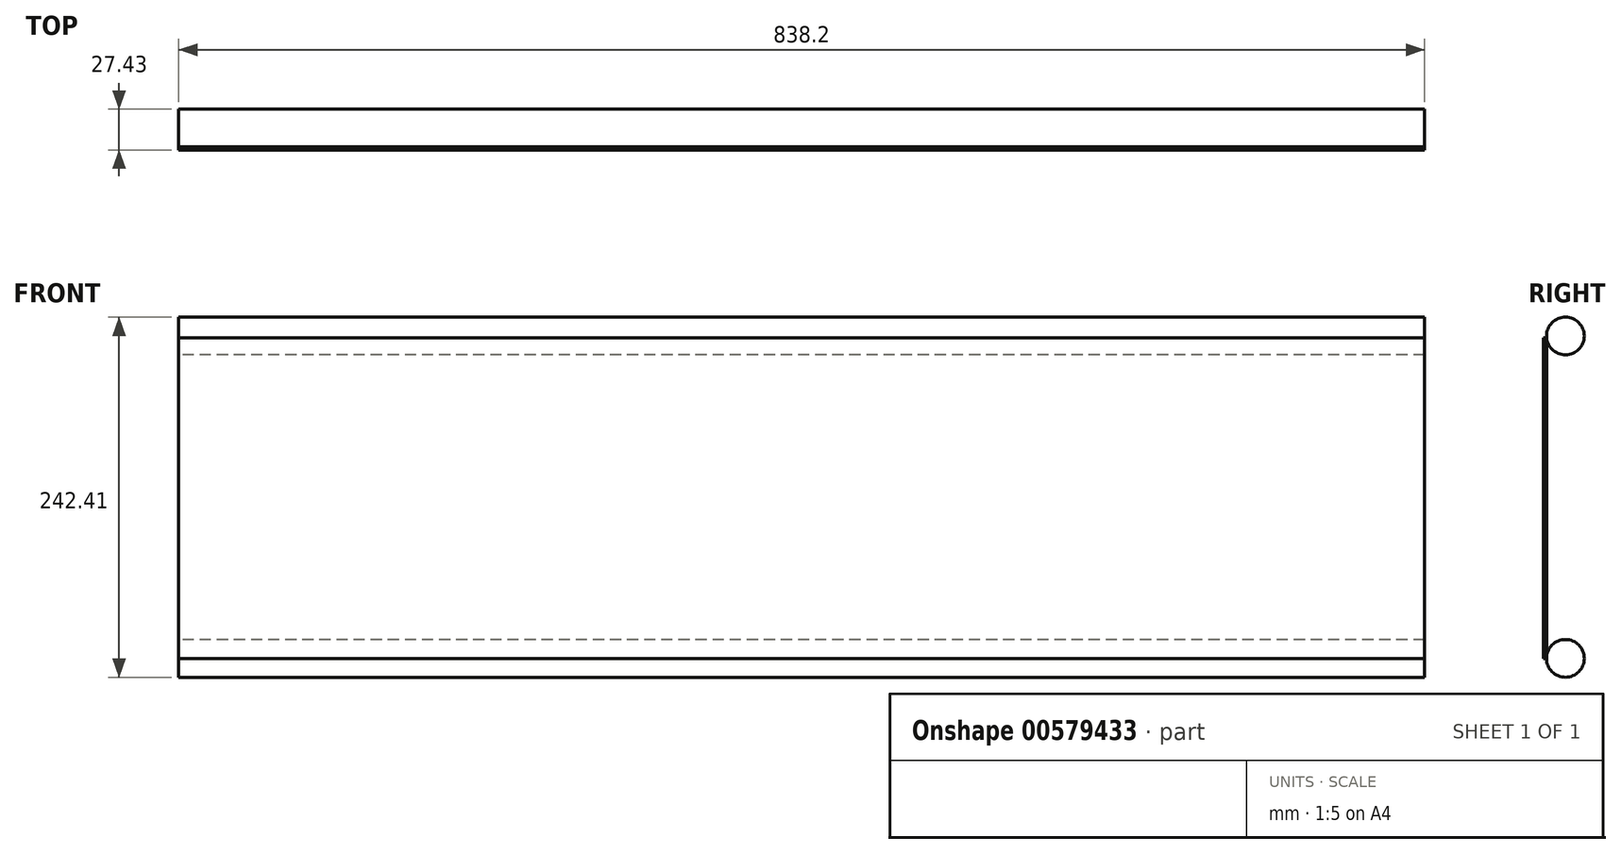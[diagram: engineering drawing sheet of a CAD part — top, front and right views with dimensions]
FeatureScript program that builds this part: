
annotation { "Feature Type Name" : "Feature", "Feature Type Description" : "" }
export const myFeature = defineFeature(function(context is Context, id is Id, definition is map)
    precondition{}
    {
        {
            var Q0;
            Q0=qCreatedBy(makeId("Front.planeOp"),FACE);
            var sketch = newSketch(context, id + "F0", { "sketchPlane" : qUnion([Q0])});
            skLineSegment(sketch, "E0.bottom", {"start": v(-293.76, 115.35) * mm, "end": v(544.44, 115.35) * mm});
            skLineSegment(sketch, "E0.top", {"start": v(-293.76, -100.55) * mm, "end": v(544.44, -100.55) * mm});
            skLineSegment(sketch, "E0.left", {"start": v(-293.76, 115.35) * mm, "end": v(-293.76, -100.55) * mm});
            skLineSegment(sketch, "E0.right", {"start": v(544.44, 115.35) * mm, "end": v(544.44, -100.55) * mm});
            skSolve(sketch);
        }
        {
            var Q0;
            Q0=makeQuery(id+"F0.imprint","IMPRINT",FACE,{"disambiguationData":[TD([[makeQuery(id+"F0.imprint","IMPRINT",EDGE,{"derivedFrom":sQuery(id+"F0.wireOp",EDGE,"E0.bottom")}),-1.0]])]});
            extrude(context, id + "F1", {"entities" : qUnion([Q0]), "depth" : 2.03 * mm, "offsetDistance" : 25.4 * mm});
        }
        {
            var Q0;
            Q0=makeQuery(id+"F1.opExtrude","SWEPT_FACE",FACE,{"disambiguationData":[OSD([sQuery(id+"F0.wireOp",EDGE,"E0.left")])]});
            var sketch = newSketch(context, id + "F2", { "sketchPlane" : qUnion([Q0])});
            skCircle(sketch, "E1", {"center": v(-12.7, -100.55) * mm, "radius": 12.7 * mm});
            skCircle(sketch, "E2", {"center": v(-12.7, 116.46) * mm, "radius": 12.7 * mm});
            skSolve(sketch);
        }
        {
            var Q0;
            Q0 = qSketchRegion(id + "F2", true);
            extrude(context, id + "F3", {"entities" : qUnion([Q0]), "oppositeDirection" : true, "depth" : 838.2 * mm, "offsetDistance" : 25.4 * mm});
        }
    });
